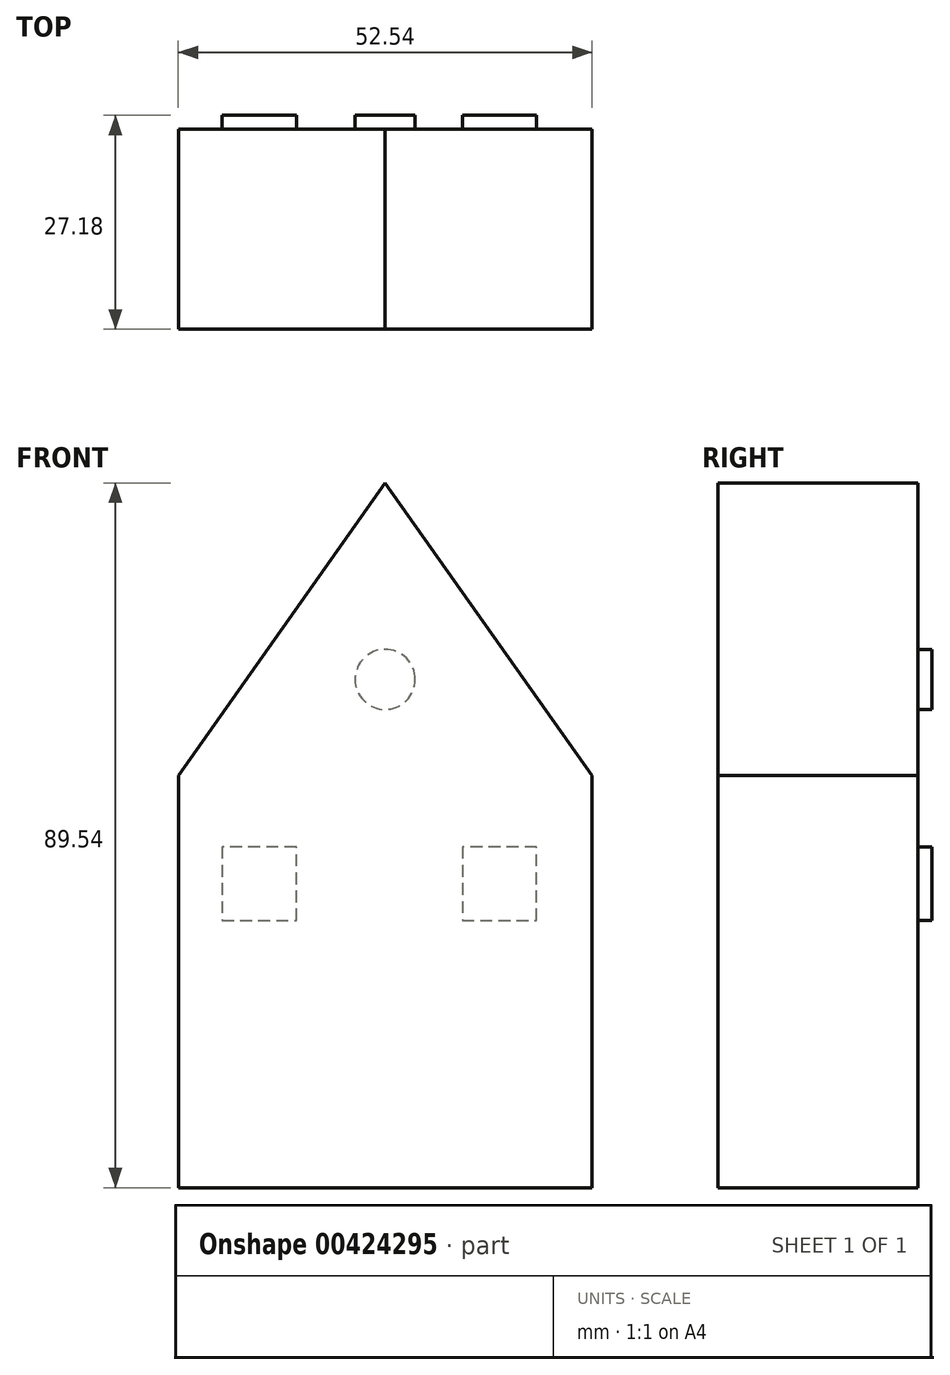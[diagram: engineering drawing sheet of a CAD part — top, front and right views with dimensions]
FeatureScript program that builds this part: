
annotation { "Feature Type Name" : "Feature", "Feature Type Description" : "" }
export const myFeature = defineFeature(function(context is Context, id is Id, definition is map)
    precondition{}
    {
        {
            var Q0;
            Q0=qCreatedBy(makeId("Front.planeOp"),FACE);
            var sketch = newSketch(context, id + "F0", { "sketchPlane" : qUnion([Q0])});
            skLineSegment(sketch, "E0", {"start": v(-26.27, 18.4) * mm, "end": v(-26.27, -33.95) * mm});
            skLineSegment(sketch, "E1", {"start": v(-26.27, -33.95) * mm, "end": v(26.27, -33.95) * mm});
            skLineSegment(sketch, "E2", {"start": v(26.27, -33.95) * mm, "end": v(26.27, 18.4) * mm});
            skLineSegment(sketch, "E3", {"start": v(26.27, 18.4) * mm, "end": v(-26.27, 18.4) * mm});
            skLineSegment(sketch, "E4", {"start": v(-26.27, 18.4) * mm, "end": v(0, 55.6) * mm});
            skPoint(sketch, "E4.endSnap0", {"position": v(0, 18.4) * mm});
            skLineSegment(sketch, "E5", {"start": v(0, 55.6) * mm, "end": v(26.27, 18.4) * mm});
            skSolve(sketch);
        }
        {
            var Q0;
            Q0=qCreatedBy(makeId("Front.planeOp"),FACE);
            var sketch = newSketch(context, id + "F1", { "sketchPlane" : qUnion([Q0])});
            skLineSegment(sketch, "E6", {"start": v(-4.62, -34.13) * mm, "end": v(-4.62, -17.48) * mm});
            skLineSegment(sketch, "E7", {"start": v(-4.62, -17.48) * mm, "end": v(4.44, -17.48) * mm});
            skLineSegment(sketch, "E8", {"start": v(4.44, -17.48) * mm, "end": v(4.44, -34.13) * mm});
            skLineSegment(sketch, "E9", {"start": v(-20.72, 9.34) * mm, "end": v(-20.72, 0) * mm});
            skLineSegment(sketch, "E10", {"start": v(-20.72, 0) * mm, "end": v(-11.28, 0) * mm});
            skLineSegment(sketch, "E11", {"start": v(-11.28, 0) * mm, "end": v(-11.28, 9.34) * mm});
            skLineSegment(sketch, "E12", {"start": v(-11.28, 9.34) * mm, "end": v(-20.72, 9.34) * mm});
            skLineSegment(sketch, "E13", {"start": v(9.8, 0) * mm, "end": v(19.24, 0) * mm});
            skLineSegment(sketch, "E14", {"start": v(19.24, 0) * mm, "end": v(19.24, 9.34) * mm});
            skLineSegment(sketch, "E15", {"start": v(19.24, 9.34) * mm, "end": v(9.8, 9.34) * mm});
            skLineSegment(sketch, "E16", {"start": v(9.8, 9.34) * mm, "end": v(9.8, 0) * mm});
            skCircle(sketch, "E17", {"center": v(0, 30.62) * mm, "radius": 3.81 * mm});
            skSolve(sketch);
        }
        {
            var Q0;
            Q0 = qSketchRegion(id + "F0", true);
            extrude(context, id + "F2", {"entities" : qUnion([Q0]), "depth" : 25.4 * mm});
        }
        {
            var Q0;
            Q0 = qSketchRegion(id + "F1", true);
            extrude(context, id + "F3", {"entities" : qUnion([Q0]), "operationType" : NewBodyOperationType.ADD, "oppositeDirection" : true, "depth" : 1.78 * mm});
        }
    });
